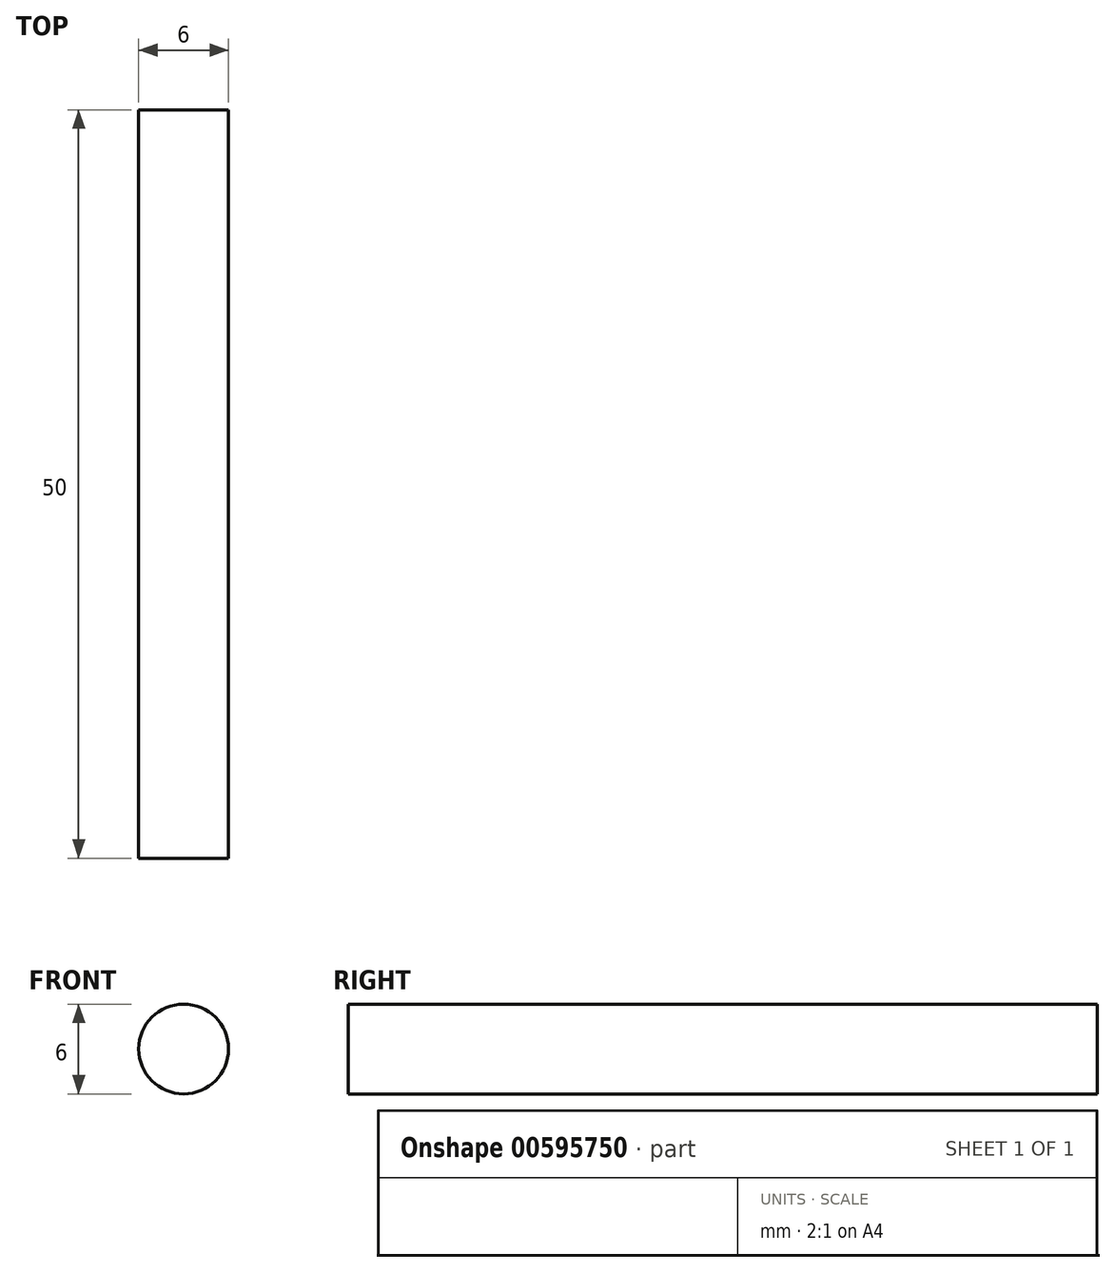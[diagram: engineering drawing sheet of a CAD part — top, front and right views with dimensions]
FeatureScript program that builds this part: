
annotation { "Feature Type Name" : "Feature", "Feature Type Description" : "" }
export const myFeature = defineFeature(function(context is Context, id is Id, definition is map)
    precondition{}
    {
        {
            var Q0;
            Q0=qCreatedBy(makeId("Front.planeOp"),FACE);
            var sketch = newSketch(context, id + "F0", { "sketchPlane" : qUnion([Q0])});
            skCircle(sketch, "E0", {"center": v(0, 0) * mm, "radius": 3 * mm});
            skSolve(sketch);
        }
        {
            var Q0;
            Q0=makeQuery(id+"F0.imprint","IMPRINT",FACE,{"disambiguationData":[TD([[makeQuery(id+"F0.imprint","IMPRINT",EDGE,{"derivedFrom":sQuery(id+"F0.wireOp",EDGE,"E0")}),1.0]])]});
            extrude(context, id + "F1", {"entities" : qUnion([Q0]), "depth" : 50 * mm, "offsetDistance" : 25 * mm, "symmetric" : true});
        }
    });
